# Revit family: Vitra_Frame_CounterTopWashBasin_5651B401-0016
name_source: partatom
category: Plumbing Fixtures
revit_build: Autodesk Revit 2017 (Build: 20160225_1515(x64)
units: mm (PartAtom-declared; Revit-internal decimal feet)

## family parameters
Cut with Voids When Loaded = No
Host = Face
OmniClass Number = 23.45.05.14.14
OmniClass Title = Sinks/Lavatories
Part Type = Normal
Room Calculation Point = No
Round Connector Dimension = Use Diameter
Shared = Yes

## types (4) — shared parameters
BIMobject category = Sanitary - Basins
CW Connection = No
Default Elevation = 800 mm  [stored 2.62467 ft]
Description = VitrA Frame Round Inset Bowl
Design country = Turkey
HW Connection = No
IFC Classification = Sanitary Terminal
Main Material = Ceramic
Manufacturer = Vitra
Manufacturer name = Vitra
Masterformat 2014 Code = 22 41 16
Masterformat 2014 Description = Residential Lavatories and Sinks
MountingType = Counter Top
NBS Referans Code = 35-65-70-94
NBS Referans Description = Wash Basin Systems
Nominal Depth = 390 mm  [stored 1.27953 ft]
NominalHeight = 150 mm
NominalWidth = 390 mm  [stored 1.27953 ft]
OmniClass Code = 23.45.05.14.14
OmniClass Description = Sinks/Lavatories
Product certification = https://vitraglobal.com
Product data url = https://www.vitra.co.uk
Product family = Counter Top Washbasins
Product group = Frame
Technical description = https://www.vitra.co.uk
UNSPSC Code = 301815
URL = https://vitraglobal.com
Uniclass 1.4 Code = L7212
Uniclass 1.4 Description = Washbasins
Uniclass 2.0 Code = SS-35-65-70-94
Uniclass 2.0 Description = Sanitary Dispensing And Disposal Units
Uniclass 2015 Code = Pr_40_20_96_81
Uniclass 2015 Name = Wash basins, Sinks and troughs
Uniformat II Code = D2010
Uniformat II Description = Plumbing Fixtures
Vent Connection = No
Warranty Period (Year) = 10 Years
Waste Connection = Yes
Weight Net (kg) = 6,950
Youtube = https://www.youtube.com
zero-valued in all types: Cost

## per-type parameters (varying)
| type | Article No. (default) | Color | Model | Product SKU | Secondary Material |
| WashBasin(CounterTop)-Vitra-FrameSeries(MattWhite)_5651B401-0016 | 5651B401-0016 | Matte White | 5651B401-0016 | 5651B401-0016 | Vitra-Ceramic-Matt White |
| WashBasin(CounterTop)-Vitra-FrameSeries(White)_5651B403-0016 | 5651B403-0016 | White | 5651B403-0016 | 5651B403-0016 | Vitra-Ceramic-White |
| WashBasin(CounterTop)-Vitra-FrameSeries(Black)_5651B470-0016 | 5651B470-0016 | Black | 5651B470-0016 | 5651B470-0016 | Vitra-Ceramic-Black |
| WashBasin(CounterTop)-Vitra-FrameSeries(MatteBlack)_5651B483-0016 | 5651B483-0016 | Matte Black | 5651B483-0016 | 5651B483-0016 | Vitra-Ceramic-MattBlack |

note: [stored X ft] marks values corroborated as IEEE doubles in the binary element streams (Revit-internal decimal feet)

## geometry (parser evidence)
native form markers: Sweep x3
no freeform markers — native parametric forms only
